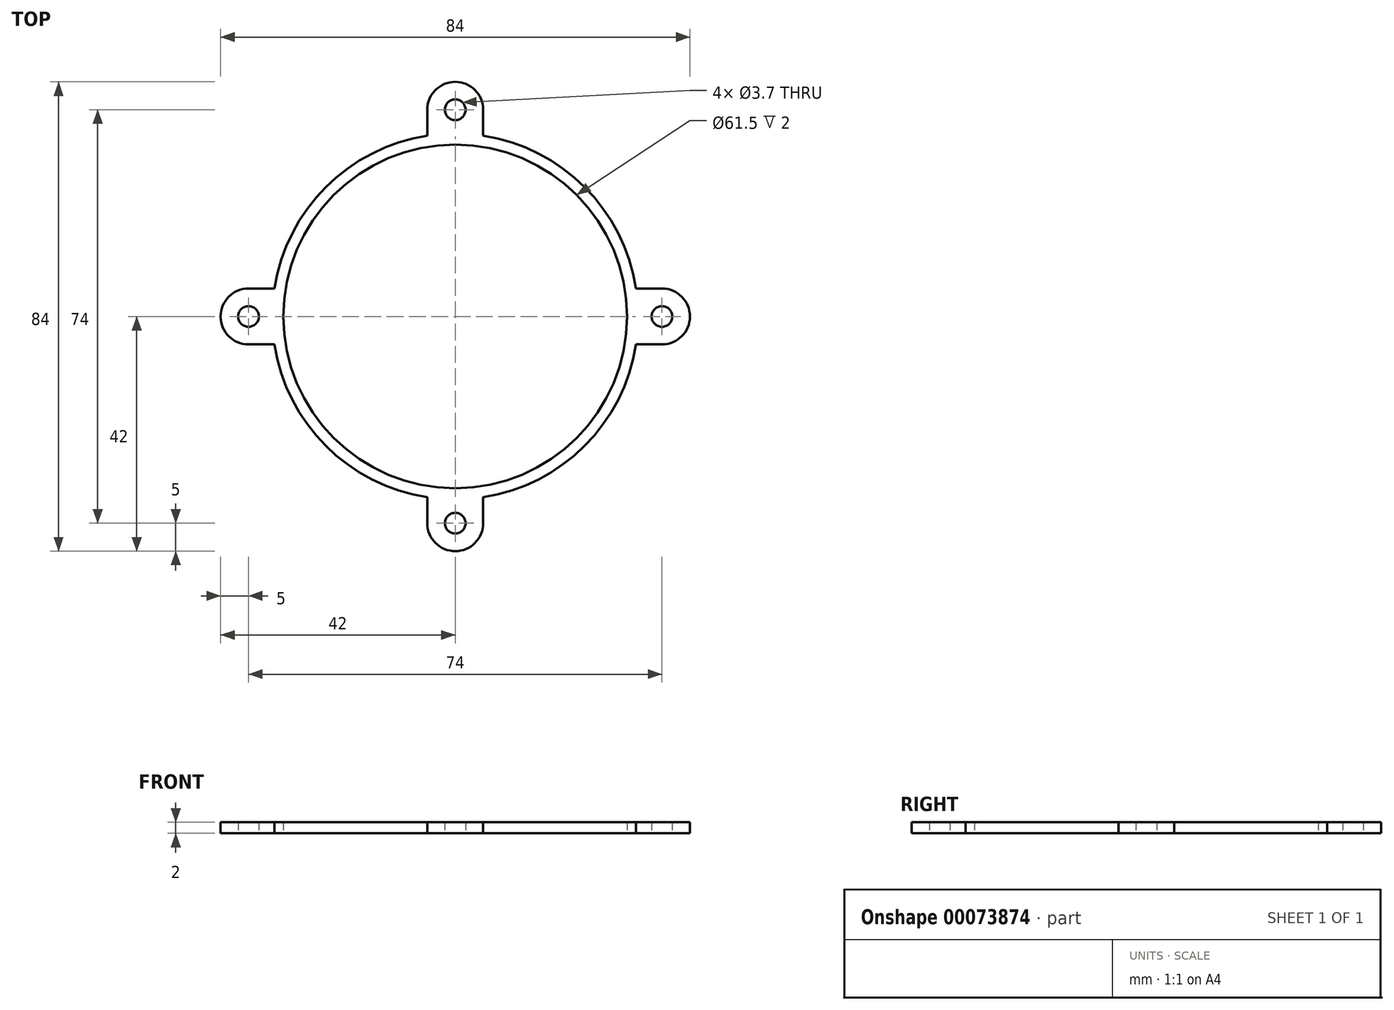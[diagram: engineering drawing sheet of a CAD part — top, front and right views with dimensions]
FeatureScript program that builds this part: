
annotation { "Feature Type Name" : "Feature", "Feature Type Description" : "" }
export const myFeature = defineFeature(function(context is Context, id is Id, definition is map)
    precondition{}
    {
        {
            var Q0;
            Q0=qCreatedBy(makeId("Top.planeOp"),FACE);
            var sketch = newSketch(context, id + "F0", { "sketchPlane" : qUnion([Q0])});
            skCircle(sketch, "E0", {"center": v(0, 0) * mm, "radius": 32.75 * mm});
            skCircle(sketch, "E1", {"center": v(0, 0) * mm, "radius": 30.75 * mm});
            skCircle(sketch, "E2", {"center": v(0, 37) * mm, "radius": 5 * mm});
            skLineSegment(sketch, "E3", {"start": v(-5, 37) * mm, "end": v(-5, 32.37) * mm});
            skLineSegment(sketch, "E4", {"start": v(5, 37) * mm, "end": v(5, 32.37) * mm});
            skCircle(sketch, "E5", {"center": v(0, 37) * mm, "radius": 1.85 * mm});
            skLineSegment(sketch, "E6.MirrorCS", {"start": v(-5, -37) * mm, "end": v(-5, -32.37) * mm});
            skCircle(sketch, "E7.MirrorC", {"center": v(0, -37) * mm, "radius": 1.85 * mm});
            skLineSegment(sketch, "E8.MirrorCS", {"start": v(5, -37) * mm, "end": v(5, -32.37) * mm});
            skCircle(sketch, "E9.MirrorC", {"center": v(0, -37) * mm, "radius": 5 * mm});
            skCircle(sketch, "E10", {"center": v(-37, 0) * mm, "radius": 5 * mm});
            skCircle(sketch, "E11", {"center": v(-37, 0) * mm, "radius": 1.85 * mm});
            skLineSegment(sketch, "E12", {"start": v(-37, 5) * mm, "end": v(-32.37, 5) * mm});
            skLineSegment(sketch, "E13", {"start": v(-37, -5) * mm, "end": v(-32.37, -5) * mm});
            skLineSegment(sketch, "E14.MirrorCS", {"start": v(37, 5) * mm, "end": v(32.37, 5) * mm});
            skCircle(sketch, "E15.MirrorC", {"center": v(37, 0) * mm, "radius": 1.85 * mm});
            skLineSegment(sketch, "E16.MirrorCS", {"start": v(37, -5) * mm, "end": v(32.37, -5) * mm});
            skCircle(sketch, "E17.MirrorC", {"center": v(37, 0) * mm, "radius": 5 * mm});
            skSolve(sketch);
        }
        {
            var Q0;
            Q0=qSketchRegion(id+"F0",true);
            var Q1;
            {var subQ0=sQuery(id+"F0.wireOp",EDGE,"E2");var subQ1=sQuery(id+"F0.wireOp",EDGE,"E0");var subQ2=makeQuery(id+"F0.imprint","INTERSECT",VERTEX,{"disambiguationData":[OD(0.0)],"derivedFrom":[subQ1,subQ0]});Q1=makeQuery(id+"F0.imprint","IMPRINT",FACE,{"disambiguationData":[TD([[makeQuery(id+"F0.imprint","IMPRINT",EDGE,{"disambiguationData":[TD([[subQ2,-1.0]])],"derivedFrom":subQ1}),1.0]])]});}
            var Q2;
            {var subQ0=sQuery(id+"F0.wireOp",EDGE,"E10");var subQ1=sQuery(id+"F0.wireOp",EDGE,"E0");var subQ2=makeQuery(id+"F0.imprint","INTERSECT",VERTEX,{"disambiguationData":[OD(0.0)],"derivedFrom":[subQ1,subQ0]});Q2=makeQuery(id+"F0.imprint","IMPRINT",FACE,{"disambiguationData":[TD([[makeQuery(id+"F0.imprint","IMPRINT",EDGE,{"disambiguationData":[TD([[subQ2,-1.0]])],"derivedFrom":subQ1}),1.0]])]});}
            var Q3;
            {var subQ0=sQuery(id+"F0.wireOp",EDGE,"E9.MirrorC");var subQ1=sQuery(id+"F0.wireOp",EDGE,"E0");var subQ2=makeQuery(id+"F0.imprint","INTERSECT",VERTEX,{"disambiguationData":[OD(0.0)],"derivedFrom":[subQ1,subQ0]});Q3=makeQuery(id+"F0.imprint","IMPRINT",FACE,{"disambiguationData":[TD([[makeQuery(id+"F0.imprint","IMPRINT",EDGE,{"disambiguationData":[TD([[subQ2,-1.0]])],"derivedFrom":subQ1}),1.0]])]});}
            var Q4;
            {var subQ0=sQuery(id+"F0.wireOp",EDGE,"E17.MirrorC");var subQ1=sQuery(id+"F0.wireOp",EDGE,"E0");var subQ2=makeQuery(id+"F0.imprint","INTERSECT",VERTEX,{"disambiguationData":[OD(0.0)],"derivedFrom":[subQ1,subQ0]});Q4=makeQuery(id+"F0.imprint","IMPRINT",FACE,{"disambiguationData":[TD([[makeQuery(id+"F0.imprint","IMPRINT",EDGE,{"disambiguationData":[TD([[subQ2,1.0]])],"derivedFrom":subQ1}),1.0]])]});}
            extrude(context, id + "F1", {"entities" : qUnion([Q0, Q1, Q2, Q3, Q4]), "depth" : 2 * mm});
        }
    });
